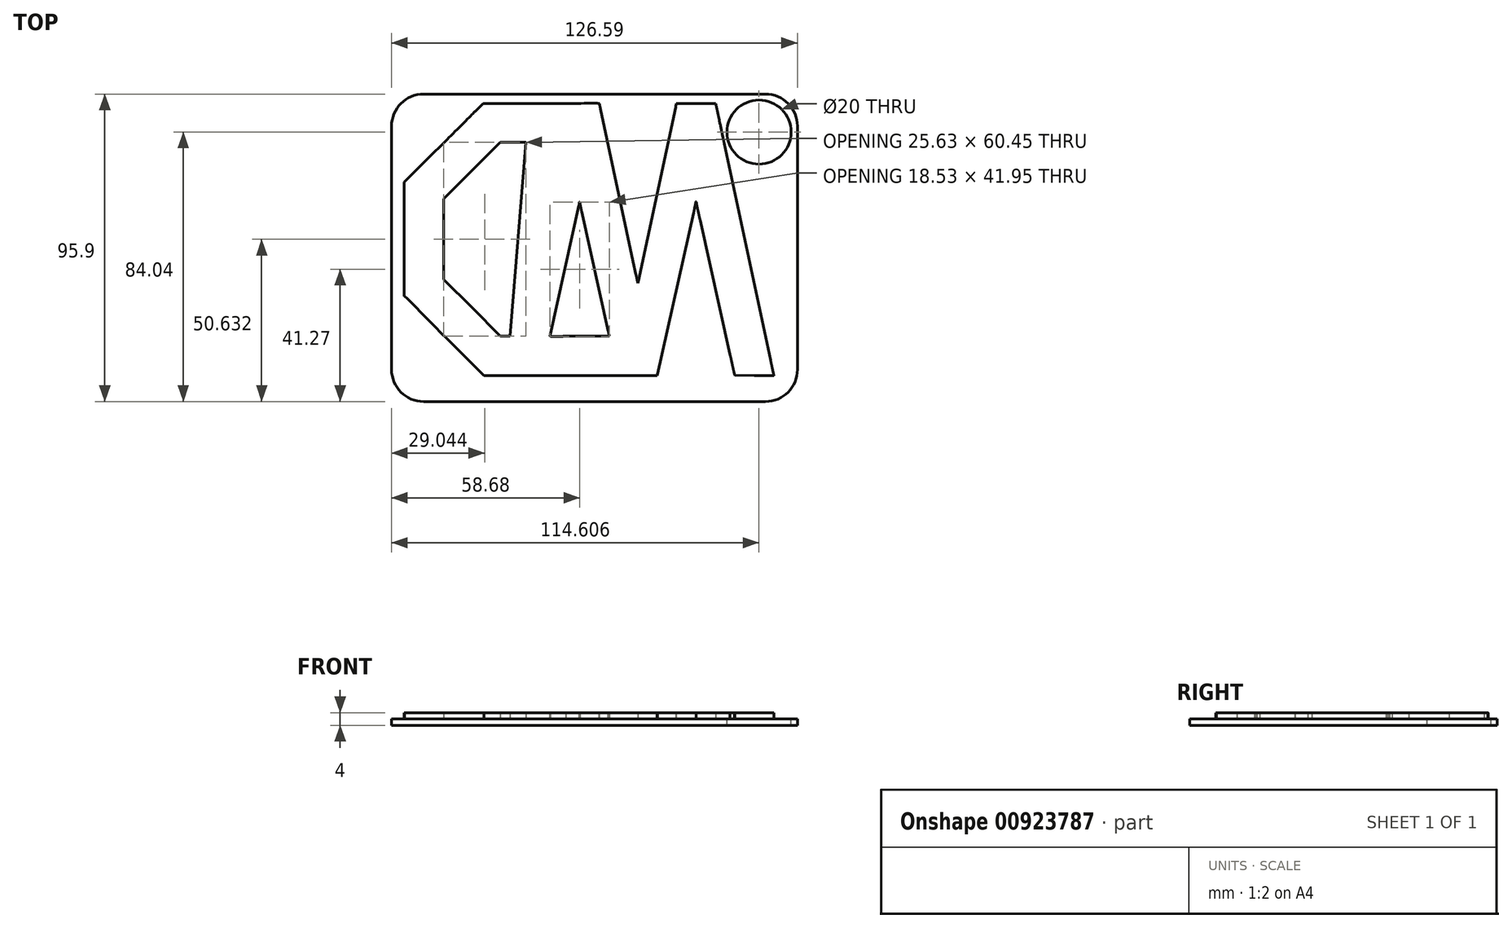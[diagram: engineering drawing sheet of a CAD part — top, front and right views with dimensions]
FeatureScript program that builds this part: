
annotation { "Feature Type Name" : "Feature", "Feature Type Description" : "" }
export const myFeature = defineFeature(function(context is Context, id is Id, definition is map)
    precondition{}
    {
        {
            var Q0;
            Q0=qCreatedBy(makeId("Top.planeOp"),FACE);
            var sketch = newSketch(context, id + "F0", { "sketchPlane" : qUnion([Q0])});
            skLineSegment(sketch, "E0", {"start": v(-57.61, 21.78) * mm, "end": v(-57.6, 39.54) * mm});
            skLineSegment(sketch, "E1", {"start": v(-57.6, 39.54) * mm, "end": v(-47.68, 49.45) * mm});
            skLineSegment(sketch, "E2", {"start": v(-35.4, 61.75) * mm, "end": v(-33.03, 64.14) * mm});
            skLineSegment(sketch, "E3", {"start": v(-33.03, 64.14) * mm, "end": v(-14.89, 64.14) * mm});
            skLineSegment(sketch, "E4", {"start": v(15.12, 8.6) * mm, "end": v(15.23, 8.04) * mm});
            skLineSegment(sketch, "E5", {"start": v(15.23, 8.04) * mm, "end": v(15.34, 8.55) * mm});
            skLineSegment(sketch, "E6", {"start": v(27.17, 63.82) * mm, "end": v(27.22, 64.14) * mm});
            skLineSegment(sketch, "E7", {"start": v(27.22, 64.14) * mm, "end": v(33.39, 64.14) * mm});
            skLineSegment(sketch, "E8", {"start": v(33.39, 64.14) * mm, "end": v(39.56, 64.14) * mm});
            skLineSegment(sketch, "E9", {"start": v(39.56, 64.14) * mm, "end": v(39.7, 63.44) * mm});
            skLineSegment(sketch, "E10", {"start": v(51.54, -20.68) * mm, "end": v(45.48, -20.66) * mm});
            skLineSegment(sketch, "E11", {"start": v(45.48, -20.66) * mm, "end": v(45.42, -20.45) * mm});
            skLineSegment(sketch, "E12", {"start": v(21.37, -20.38) * mm, "end": v(21.28, -20.7) * mm});
            skLineSegment(sketch, "E13", {"start": v(21.28, -20.7) * mm, "end": v(15.76, -20.72) * mm});
            skLineSegment(sketch, "E14", {"start": v(-11.25, -20.74) * mm, "end": v(-32.73, -20.74) * mm});
            skLineSegment(sketch, "E15", {"start": v(-32.73, -20.74) * mm, "end": v(-40.08, -13.39) * mm});
            skLineSegment(sketch, "E16", {"start": v(-40.08, -13.39) * mm, "end": v(-40.08, -13.39) * mm});
            skLineSegment(sketch, "E17", {"start": v(0.22, -8.42) * mm, "end": v(6.38, -8.42) * mm});
            skLineSegment(sketch, "E18", {"start": v(6.38, -8.42) * mm, "end": v(6.26, -7.98) * mm});
            skLineSegment(sketch, "E19", {"start": v(-19.7, 52.03) * mm, "end": v(-27.72, 52.03) * mm});
            skLineSegment(sketch, "E20", {"start": v(-27.72, 52.03) * mm, "end": v(-36.52, 43.18) * mm});
            skLineSegment(sketch, "E21", {"start": v(-36.52, 43.18) * mm, "end": v(-45.32, 34.33) * mm});
            skLineSegment(sketch, "E22", {"start": v(-45.34, 9.3) * mm, "end": v(-36.49, 0.44) * mm});
            skLineSegment(sketch, "E23", {"start": v(-36.49, 0.44) * mm, "end": v(-27.63, -8.42) * mm});
            skLineSegment(sketch, "E24", {"start": v(-27.63, -8.42) * mm, "end": v(-26.12, -8.42) * mm});
            skLineSegment(sketch, "E25", {"start": v(-26.12, -8.42) * mm, "end": v(-24.6, -8.42) * mm});
            skFitSpline(sketch, "E26", {"points": [v(-40.08, -13.39) * mm, v(-52.2, -1.24) * mm, v(-57.49, 4.02) * mm, v(-57.56, 4.02) * mm]});
            skFitSpline(sketch, "E27", {"points": [v(-57.56, 4.02) * mm, v(-57.6, 4.02) * mm, v(-57.62, 12.01) * mm, v(-57.61, 21.78) * mm]});
            skFitSpline(sketch, "E28", {"points": [v(-47.68, 49.45) * mm, v(-42.23, 54.9) * mm, v(-36.7, 60.44) * mm, v(-35.4, 61.75) * mm]});
            skFitSpline(sketch, "E29", {"points": [v(-14.89, 64.14) * mm, v(-4.9, 64.14) * mm, v(3.26, 64.1) * mm, v(3.26, 64.07) * mm]});
            skFitSpline(sketch, "E30", {"points": [v(3.26, 64.07) * mm, v(3.26, 64.04) * mm, v(3.41, 63.28) * mm, v(3.6, 62.4) * mm]});
            skFitSpline(sketch, "E31", {"points": [v(13.8, 14.86) * mm, v(13.9, 14.3) * mm, v(14.1, 13.36) * mm, v(14.65, 10.8) * mm]});
            skFitSpline(sketch, "E32", {"points": [v(14.65, 10.8) * mm, v(14.73, 10.45) * mm, v(14.84, 9.93) * mm, v(14.9, 9.65) * mm]});
            skFitSpline(sketch, "E33", {"points": [v(14.9, 9.65) * mm, v(14.97, 9.37) * mm, v(15.06, 8.9) * mm, v(15.12, 8.6) * mm]});
            skFitSpline(sketch, "E34", {"points": [v(27, 63) * mm, v(27.07, 63.27) * mm, v(27.14, 63.64) * mm, v(27.17, 63.82) * mm]});
            skFitSpline(sketch, "E35", {"points": [v(39.7, 63.44) * mm, v(39.77, 63.05) * mm, v(39.88, 62.5) * mm, v(39.95, 62.19) * mm]});
            skFitSpline(sketch, "E36", {"points": [v(39.95, 62.19) * mm, v(40.01, 61.89) * mm, v(40.13, 61.35) * mm, v(40.2, 61) * mm]});
            skFitSpline(sketch, "E37", {"points": [v(40.2, 61) * mm, v(40.4, 60) * mm, v(40.85, 57.94) * mm, v(41.57, 54.55) * mm]});
            skFitSpline(sketch, "E38", {"points": [v(41.57, 54.55) * mm, v(41.64, 54.23) * mm, v(41.75, 53.72) * mm, v(41.81, 53.4) * mm]});
            skFitSpline(sketch, "E39", {"points": [v(41.81, 53.4) * mm, v(41.88, 53.09) * mm, v(42.06, 52.28) * mm, v(42.2, 51.6) * mm]});
            skFitSpline(sketch, "E40", {"points": [v(56.63, -15.87) * mm, v(56.7, -16.18) * mm, v(56.9, -17.1) * mm, v(57.06, -17.9) * mm]});
            skFitSpline(sketch, "E41", {"points": [v(57.06, -17.9) * mm, v(57.22, -18.72) * mm, v(57.42, -19.6) * mm, v(57.49, -19.87) * mm]});
            skFitSpline(sketch, "E42", {"points": [v(57.49, -19.87) * mm, v(57.55, -20.14) * mm, v(57.61, -20.44) * mm, v(57.61, -20.53) * mm]});
            skFitSpline(sketch, "E43", {"points": [v(57.61, -20.53) * mm, v(57.61, -20.7) * mm, v(57.58, -20.7) * mm, v(51.54, -20.68) * mm]});
            skFitSpline(sketch, "E44", {"points": [v(45.42, -20.45) * mm, v(45.35, -20.2) * mm, v(45.2, -19.52) * mm, v(44.83, -17.86) * mm]});
            skFitSpline(sketch, "E45", {"points": [v(44.83, -17.86) * mm, v(44.41, -15.98) * mm, v(44.24, -15.22) * mm, v(43.96, -14.14) * mm]});
            skFitSpline(sketch, "E46", {"points": [v(34.64, 27.81) * mm, v(34.57, 28.12) * mm, v(34.4, 28.92) * mm, v(34.25, 29.6) * mm]});
            skFitSpline(sketch, "E47", {"points": [v(34.25, 29.6) * mm, v(34.1, 30.27) * mm, v(33.92, 31.07) * mm, v(33.85, 31.37) * mm]});
            skFitSpline(sketch, "E48", {"points": [v(33.85, 31.37) * mm, v(33.79, 31.67) * mm, v(33.67, 32.26) * mm, v(33.6, 32.68) * mm]});
            skFitSpline(sketch, "E49", {"points": [v(33.6, 32.68) * mm, v(33.52, 33.1) * mm, v(33.43, 33.48) * mm, v(33.4, 33.51) * mm]});
            skFitSpline(sketch, "E50", {"points": [v(33.4, 33.51) * mm, v(33.36, 33.55) * mm, v(33.3, 33.34) * mm, v(33.24, 33.05) * mm]});
            skFitSpline(sketch, "E51", {"points": [v(33.24, 33.05) * mm, v(33.2, 32.75) * mm, v(33.12, 32.36) * mm, v(33.07, 32.17) * mm]});
            skFitSpline(sketch, "E52", {"points": [v(33.07, 32.17) * mm, v(33.01, 31.99) * mm, v(32.94, 31.6) * mm, v(32.9, 31.33) * mm]});
            skFitSpline(sketch, "E53", {"points": [v(32.9, 31.33) * mm, v(32.85, 31.05) * mm, v(32.73, 30.46) * mm, v(32.64, 30.01) * mm]});
            skFitSpline(sketch, "E54", {"points": [v(15.76, -20.72) * mm, v(12.72, -20.72) * mm, v(0.57, -20.73) * mm, v(-11.25, -20.74) * mm]});
            skFitSpline(sketch, "E55", {"points": [v(6.26, -7.98) * mm, v(6.2, -7.74) * mm, v(6.08, -7.25) * mm, v(6, -6.9) * mm]});
            skFitSpline(sketch, "E56", {"points": [v(-2.28, 30.48) * mm, v(-2.48, 31.36) * mm, v(-2.69, 32.32) * mm, v(-2.79, 32.84) * mm]});
            skFitSpline(sketch, "E57", {"points": [v(-2.79, 32.84) * mm, v(-2.88, 33.3) * mm, v(-3.01, 33.41) * mm, v(-3.01, 33.02) * mm]});
            skFitSpline(sketch, "E58", {"points": [v(-3.01, 33.02) * mm, v(-3.01, 32.93) * mm, v(-3.06, 32.64) * mm, v(-3.13, 32.38) * mm]});
            skFitSpline(sketch, "E59", {"points": [v(-12.07, -7.93) * mm, v(-12.12, -8.1) * mm, v(-12.15, -8.27) * mm, v(-12.15, -8.33) * mm]});
            skFitSpline(sketch, "E60", {"points": [v(-12.15, -8.33) * mm, v(-12.15, -8.43) * mm, v(-9.46, -8.5) * mm, v(-7.24, -8.45) * mm]});
            skFitSpline(sketch, "E61", {"points": [v(-7.24, -8.45) * mm, v(-6.52, -8.44) * mm, v(-3.16, -8.42) * mm, v(0.22, -8.42) * mm]});
            skLineSegment(sketch, "E62", {"start": v(-24.6, -8.42) * mm, "end": v(-19.7, 52.03) * mm});
            skLineSegment(sketch, "E63", {"start": v(-45.34, 9.3) * mm, "end": v(-45.32, 34.33) * mm});
            skLineSegment(sketch, "E64", {"start": v(-12.07, -7.93) * mm, "end": v(-3.13, 32.38) * mm});
            skLineSegment(sketch, "E65", {"start": v(6, -6.9) * mm, "end": v(-2.28, 30.48) * mm});
            skLineSegment(sketch, "E66", {"start": v(3.6, 62.4) * mm, "end": v(13.8, 14.86) * mm});
            skLineSegment(sketch, "E67", {"start": v(21.37, -20.38) * mm, "end": v(32.64, 30.01) * mm});
            skLineSegment(sketch, "E68", {"start": v(34.64, 27.81) * mm, "end": v(43.96, -14.14) * mm});
            skLineSegment(sketch, "E69", {"start": v(42.2, 51.6) * mm, "end": v(56.63, -15.87) * mm});
            skLineSegment(sketch, "E70", {"start": v(15.34, 8.55) * mm, "end": v(27, 63) * mm});
            skSolve(sketch);
        }
        {
            var Q0;
            Q0 = qSketchRegion(id + "F0", true);
            extrude(context, id + "F1", {"entities" : qUnion([Q0]), "depth" : 2 * mm, "offsetDistance" : 25 * mm});
        }
        {
            var Q0;
            Q0=makeQuery(id+"F1.opExtrude","CAP_FACE",FACE,{"disambiguationData":[OSD([sQuery(id+"F0.wireOp",EDGE,"E0"),sQuery(id+"F0.wireOp",EDGE,"E1"),sQuery(id+"F0.wireOp",EDGE,"E2"),sQuery(id+"F0.wireOp",EDGE,"E3"),sQuery(id+"F0.wireOp",EDGE,"E4"),sQuery(id+"F0.wireOp",EDGE,"E5"),sQuery(id+"F0.wireOp",EDGE,"E6"),sQuery(id+"F0.wireOp",EDGE,"E7"),sQuery(id+"F0.wireOp",EDGE,"E8"),sQuery(id+"F0.wireOp",EDGE,"E9"),sQuery(id+"F0.wireOp",EDGE,"E10"),sQuery(id+"F0.wireOp",EDGE,"E11"),sQuery(id+"F0.wireOp",EDGE,"E12"),sQuery(id+"F0.wireOp",EDGE,"E13"),sQuery(id+"F0.wireOp",EDGE,"E14"),sQuery(id+"F0.wireOp",EDGE,"E15"),sQuery(id+"F0.wireOp",EDGE,"E17"),sQuery(id+"F0.wireOp",EDGE,"E18"),sQuery(id+"F0.wireOp",EDGE,"E19"),sQuery(id+"F0.wireOp",EDGE,"E20"),sQuery(id+"F0.wireOp",EDGE,"E21"),sQuery(id+"F0.wireOp",EDGE,"E22"),sQuery(id+"F0.wireOp",EDGE,"E23"),sQuery(id+"F0.wireOp",EDGE,"E24"),sQuery(id+"F0.wireOp",EDGE,"E25"),sQuery(id+"F0.wireOp",EDGE,"E26"),sQuery(id+"F0.wireOp",EDGE,"E27"),sQuery(id+"F0.wireOp",EDGE,"E28"),sQuery(id+"F0.wireOp",EDGE,"E29"),sQuery(id+"F0.wireOp",EDGE,"E30"),sQuery(id+"F0.wireOp",EDGE,"E31"),sQuery(id+"F0.wireOp",EDGE,"E32"),sQuery(id+"F0.wireOp",EDGE,"E33"),sQuery(id+"F0.wireOp",EDGE,"E34"),sQuery(id+"F0.wireOp",EDGE,"E35"),sQuery(id+"F0.wireOp",EDGE,"E36"),sQuery(id+"F0.wireOp",EDGE,"E37"),sQuery(id+"F0.wireOp",EDGE,"E38"),sQuery(id+"F0.wireOp",EDGE,"E39"),sQuery(id+"F0.wireOp",EDGE,"E40"),sQuery(id+"F0.wireOp",EDGE,"E41"),sQuery(id+"F0.wireOp",EDGE,"E42"),sQuery(id+"F0.wireOp",EDGE,"E43"),sQuery(id+"F0.wireOp",EDGE,"E44"),sQuery(id+"F0.wireOp",EDGE,"E45"),sQuery(id+"F0.wireOp",EDGE,"E46"),sQuery(id+"F0.wireOp",EDGE,"E47"),sQuery(id+"F0.wireOp",EDGE,"E48"),sQuery(id+"F0.wireOp",EDGE,"E49"),sQuery(id+"F0.wireOp",EDGE,"E50"),sQuery(id+"F0.wireOp",EDGE,"E51"),sQuery(id+"F0.wireOp",EDGE,"E52"),sQuery(id+"F0.wireOp",EDGE,"E53"),sQuery(id+"F0.wireOp",EDGE,"E54"),sQuery(id+"F0.wireOp",EDGE,"E55"),sQuery(id+"F0.wireOp",EDGE,"E56"),sQuery(id+"F0.wireOp",EDGE,"E57"),sQuery(id+"F0.wireOp",EDGE,"E58"),sQuery(id+"F0.wireOp",EDGE,"E59"),sQuery(id+"F0.wireOp",EDGE,"E60"),sQuery(id+"F0.wireOp",EDGE,"E61"),sQuery(id+"F0.wireOp",EDGE,"E62"),sQuery(id+"F0.wireOp",EDGE,"E63"),sQuery(id+"F0.wireOp",EDGE,"E64"),sQuery(id+"F0.wireOp",EDGE,"E65"),sQuery(id+"F0.wireOp",EDGE,"E66"),sQuery(id+"F0.wireOp",EDGE,"E67"),sQuery(id+"F0.wireOp",EDGE,"E68"),sQuery(id+"F0.wireOp",EDGE,"E69"),sQuery(id+"F0.wireOp",EDGE,"E70")])],"isStart":true});
            var sketch = newSketch(context, id + "F2", { "sketchPlane" : qUnion([Q0])});
            skPoint(sketch, "E71.middle", {"position": v(0, 0) * mm});
            skLineSegment(sketch, "E72.bottom", {"start": v(-51.57, -67.07) * mm, "end": v(55.02, -67.07) * mm});
            skLineSegment(sketch, "E72.top", {"start": v(-51.57, 28.83) * mm, "end": v(55.02, 28.83) * mm});
            skLineSegment(sketch, "E72.left", {"start": v(-61.57, -57.07) * mm, "end": v(-61.57, 18.83) * mm});
            skLineSegment(sketch, "E72.right", {"start": v(65.02, -57.07) * mm, "end": v(65.02, 18.83) * mm});
            skPoint(sketch, "E73.visualSharp", {"position": v(-61.57, -67.07) * mm});
            skArc(sketch, "E73.filletArc", {"start": v(-61.57, -57.07) * mm, "mid": v(-58.64, -64.14) * mm, "end": v(-51.57, -67.07) * mm});
            skPoint(sketch, "E74.visualSharp", {"position": v(-61.57, 28.83) * mm});
            skArc(sketch, "E74.filletArc", {"start": v(-51.57, 28.83) * mm, "mid": v(-58.64, 25.9) * mm, "end": v(-61.57, 18.83) * mm});
            skPoint(sketch, "E75.visualSharp", {"position": v(65.02, 28.83) * mm});
            skArc(sketch, "E75.filletArc", {"start": v(65.02, 18.83) * mm, "mid": v(62.1, 25.9) * mm, "end": v(55.02, 28.83) * mm});
            skPoint(sketch, "E76.visualSharp", {"position": v(65.02, -67.07) * mm});
            skArc(sketch, "E76.filletArc", {"start": v(55.02, -67.07) * mm, "mid": v(62.1, -64.14) * mm, "end": v(65.02, -57.07) * mm});
            skSolve(sketch);
        }
        {
            var Q0;
            Q0 = qSketchRegion(id + "F2", true);
            extrude(context, id + "F3", {"entities" : qUnion([Q0]), "depth" : 2 * mm, "offsetDistance" : 25 * mm});
        }
        {
            var Q0;
            Q0=makeQuery(id+"F3.opExtrude","CAP_FACE",FACE,{"disambiguationData":[OSD([sQuery(id+"F2.wireOp",EDGE,"E72.bottom"),sQuery(id+"F2.wireOp",EDGE,"E72.top"),sQuery(id+"F2.wireOp",EDGE,"E72.left"),sQuery(id+"F2.wireOp",EDGE,"E72.right"),sQuery(id+"F2.wireOp",EDGE,"E73.filletArc"),sQuery(id+"F2.wireOp",EDGE,"E74.filletArc"),sQuery(id+"F2.wireOp",EDGE,"E75.filletArc"),sQuery(id+"F2.wireOp",EDGE,"E76.filletArc")])],"isStart":true});
            var sketch = newSketch(context, id + "F4", { "sketchPlane" : qUnion([Q0])});
            skCircle(sketch, "E77", {"center": v(53.04, 55.21) * mm, "radius": 10 * mm});
            skSolve(sketch);
        }
        {
            var Q0;
            Q0=makeQuery(id+"F4.imprint","IMPRINT",FACE,{"disambiguationData":[TD([[makeQuery(id+"F4.imprint","IMPRINT",EDGE,{"derivedFrom":sQuery(id+"F4.wireOp",EDGE,"E77")}),1.0]])]});
            extrude(context, id + "F5", {"entities" : qUnion([Q0]), "operationType" : NewBodyOperationType.REMOVE, "oppositeDirection" : true, "depth" : 2 * mm, "offsetDistance" : 25 * mm});
        }
    });
